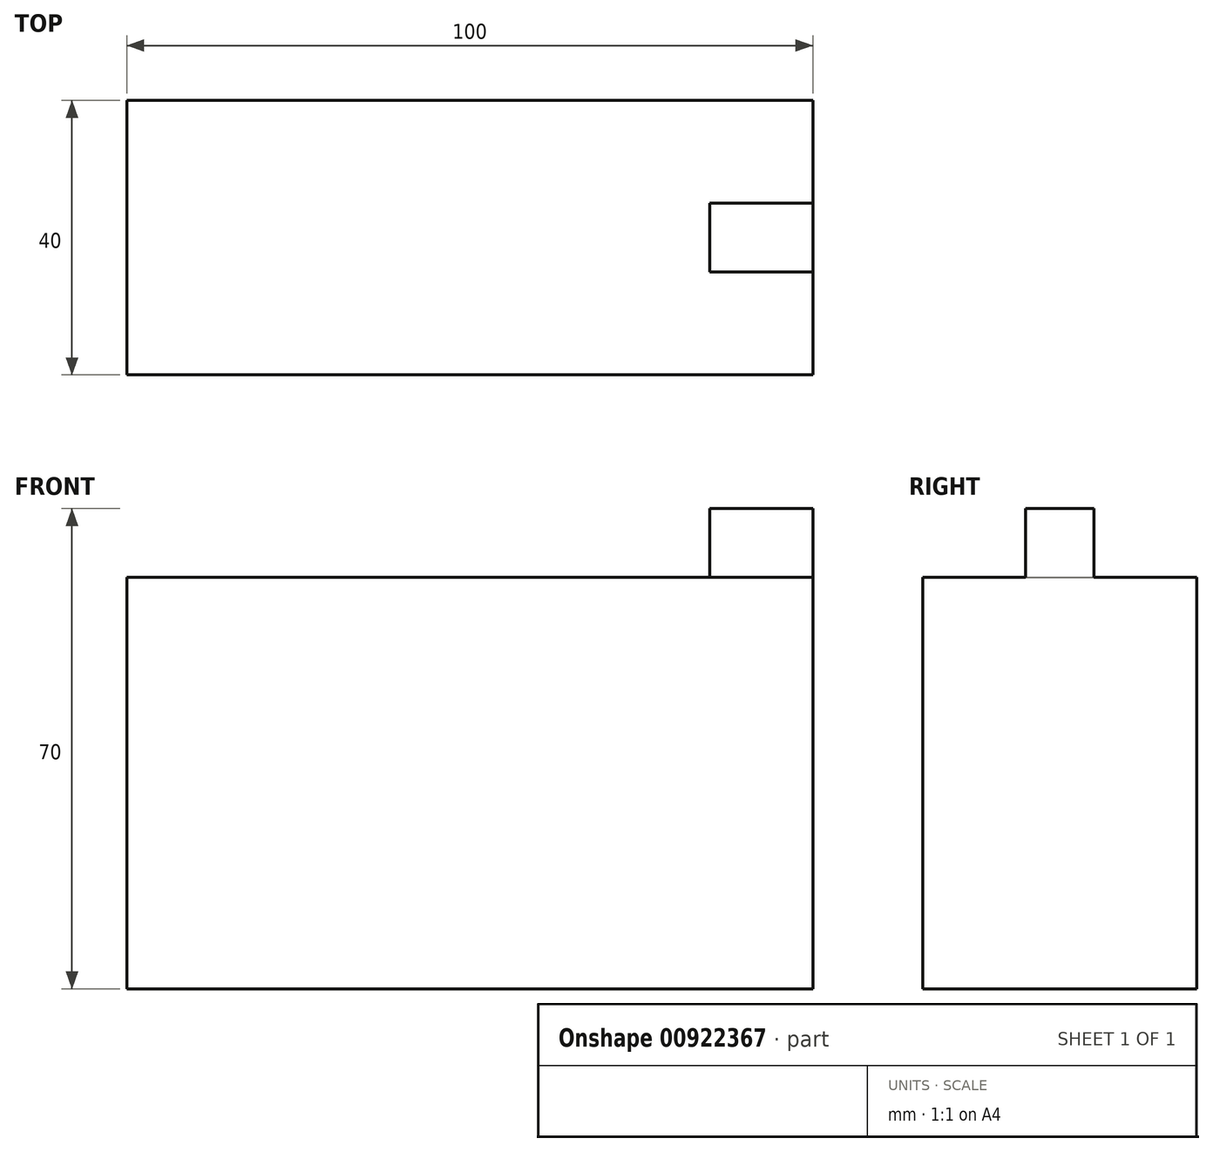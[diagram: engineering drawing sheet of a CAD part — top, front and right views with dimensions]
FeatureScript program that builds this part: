
annotation { "Feature Type Name" : "Feature", "Feature Type Description" : "" }
export const myFeature = defineFeature(function(context is Context, id is Id, definition is map)
    precondition{}
    {
        {
            var Q0;
            Q0=qCreatedBy(makeId("Top.planeOp"),FACE);
            var sketch = newSketch(context, id + "F0", { "sketchPlane" : qUnion([Q0])});
            skLineSegment(sketch, "E0.bottom", {"start": v(0, 0) * mm, "end": v(-100, 0) * mm});
            skLineSegment(sketch, "E0.top", {"start": v(0, 40) * mm, "end": v(-100, 40) * mm});
            skLineSegment(sketch, "E0.left", {"start": v(0, 0) * mm, "end": v(0, 40) * mm});
            skLineSegment(sketch, "E0.right", {"start": v(-100, 0) * mm, "end": v(-100, 40) * mm});
            skSolve(sketch);
        }
        {
            var Q0;
            Q0 = qSketchRegion(id + "F0", true);
            extrude(context, id + "F1", {"entities" : qUnion([Q0]), "endBound" : BoundingType.SYMMETRIC, "depth" : 60 * mm, "offsetDistance" : 25 * mm});
        }
        {
            var Q0;
            Q0=makeQuery(id+"F1.opExtrude","CAP_FACE",FACE,{"disambiguationData":[OSD([sQuery(id+"F0.wireOp",EDGE,"E0.bottom"),sQuery(id+"F0.wireOp",EDGE,"E0.top"),sQuery(id+"F0.wireOp",EDGE,"E0.left"),sQuery(id+"F0.wireOp",EDGE,"E0.right")])],"isStart":false});
            var sketch = newSketch(context, id + "F2", { "sketchPlane" : qUnion([Q0])});
            skLineSegment(sketch, "E1.bottom", {"start": v(0, 15) * mm, "end": v(-15, 15) * mm});
            skLineSegment(sketch, "E1.top", {"start": v(0, 25) * mm, "end": v(-15, 25) * mm});
            skLineSegment(sketch, "E1.left", {"start": v(0, 15) * mm, "end": v(0, 25) * mm});
            skLineSegment(sketch, "E1.right", {"start": v(-15, 15) * mm, "end": v(-15, 25) * mm});
            skSolve(sketch);
        }
        {
            var Q0;
            Q0 = qSketchRegion(id + "F2", true);
            extrude(context, id + "F3", {"entities" : qUnion([Q0]), "operationType" : NewBodyOperationType.ADD, "depth" : 10 * mm, "offsetDistance" : 25 * mm});
        }
    });
